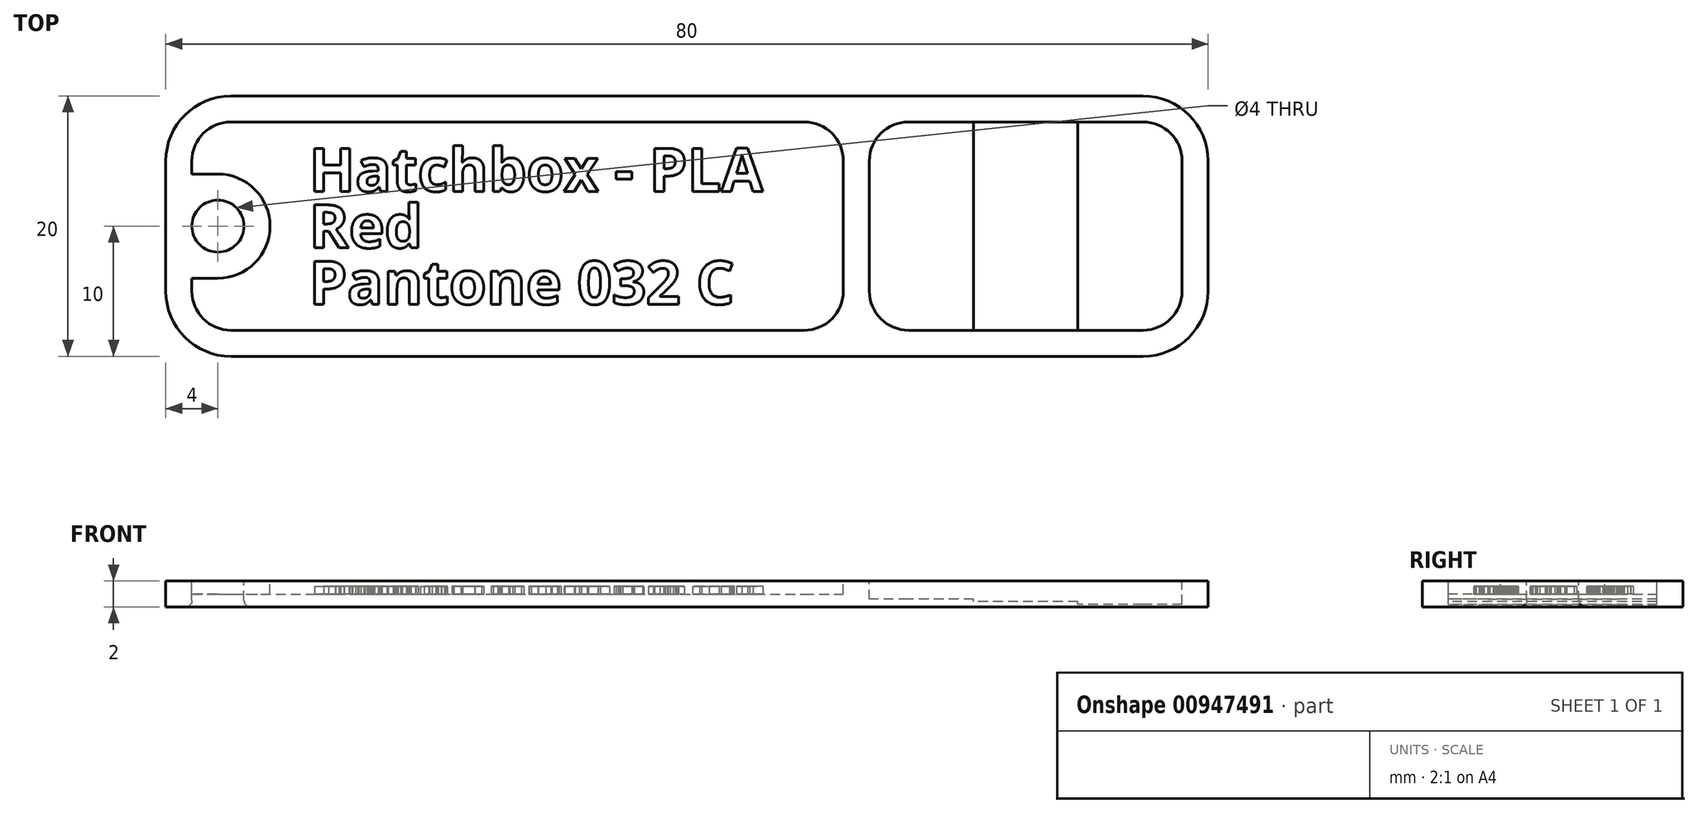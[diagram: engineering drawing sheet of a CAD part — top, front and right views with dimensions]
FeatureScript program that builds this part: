
annotation { "Feature Type Name" : "Feature", "Feature Type Description" : "" }
export const myFeature = defineFeature(function(context is Context, id is Id, definition is map)
    precondition{}
    {
        {
            var Q0;
            Q0=qCreatedBy(makeId("Top.planeOp"),FACE);
            var sketch = newSketch(context, id + "F0", { "sketchPlane" : qUnion([Q0])});
            skLineSegment(sketch, "E0.bottom", {"start": v(35, 10) * mm, "end": v(-35, 10) * mm});
            skLineSegment(sketch, "E0.top", {"start": v(35, -10) * mm, "end": v(-35, -10) * mm});
            skLineSegment(sketch, "E0.left", {"start": v(40, 5) * mm, "end": v(40, -5) * mm});
            skLineSegment(sketch, "E0.right", {"start": v(-40, 5) * mm, "end": v(-40, -5) * mm});
            skPoint(sketch, "E0.middle", {"position": v(0, 0) * mm});
            skPoint(sketch, "E1.visualSharp", {"position": v(-40, 10) * mm});
            skArc(sketch, "E1.filletArc", {"start": v(-35, 10) * mm, "mid": v(-38.54, 8.54) * mm, "end": v(-40, 5) * mm});
            skPoint(sketch, "E2.visualSharp", {"position": v(40, 10) * mm});
            skArc(sketch, "E2.filletArc", {"start": v(40, 5) * mm, "mid": v(38.54, 8.54) * mm, "end": v(35, 10) * mm});
            skPoint(sketch, "E3.visualSharp", {"position": v(40, -10) * mm});
            skArc(sketch, "E3.filletArc", {"start": v(35, -10) * mm, "mid": v(38.54, -8.54) * mm, "end": v(40, -5) * mm});
            skPoint(sketch, "E4.visualSharp", {"position": v(-40, -10) * mm});
            skArc(sketch, "E4.filletArc", {"start": v(-40, -5) * mm, "mid": v(-38.54, -8.54) * mm, "end": v(-35, -10) * mm});
            skSolve(sketch);
        }
        {
            var Q0;
            Q0=qSketchRegion(id+"F0",true);
            extrude(context, id + "F1", {"entities" : qUnion([Q0]), "offsetDistance" : 25 * mm, "depth" : 2 * mm});
        }
        {
            var Q0;
            Q0=makeQuery(id+"F1.opExtrude","CAP_FACE",FACE,{"disambiguationData":[OSD([sQuery(id+"F0.wireOp",EDGE,"E0.bottom"),sQuery(id+"F0.wireOp",EDGE,"E0.top"),sQuery(id+"F0.wireOp",EDGE,"E0.left"),sQuery(id+"F0.wireOp",EDGE,"E0.right"),sQuery(id+"F0.wireOp",EDGE,"E1.filletArc"),sQuery(id+"F0.wireOp",EDGE,"E2.filletArc"),sQuery(id+"F0.wireOp",EDGE,"E3.filletArc"),sQuery(id+"F0.wireOp",EDGE,"E4.filletArc")])],"isStart":false});
            var sketch = newSketch(context, id + "F2", { "sketchPlane" : qUnion([Q0])});
            skLineSegment(sketch, "E5.0", {"start": v(38, -5) * mm, "end": v(38, 5) * mm});
            skArc(sketch, "E5.1", {"start": v(35, -8) * mm, "mid": v(37.12, -7.12) * mm, "end": v(38, -5) * mm});
            skArc(sketch, "E5.2", {"start": v(38, 5) * mm, "mid": v(37.12, 7.12) * mm, "end": v(35, 8) * mm});
            skLineSegment(sketch, "E5.3", {"start": v(-35, -8) * mm, "end": v(9, -8) * mm});
            skLineSegment(sketch, "E5.4", {"start": v(35, 8) * mm, "end": v(17, 8) * mm});
            skArc(sketch, "E5.5", {"start": v(-35, 8) * mm, "mid": v(-37.12, 7.12) * mm, "end": v(-38, 5) * mm});
            skArc(sketch, "E5.7", {"start": v(-38, -5) * mm, "mid": v(-37.12, -7.12) * mm, "end": v(-35, -8) * mm});
            skCircle(sketch, "E6", {"center": v(-36, 0) * mm, "radius": 2 * mm, "construction": true});
            skArc(sketch, "E7.0", {"start": v(-36, -4) * mm, "mid": v(-32, 0) * mm, "end": v(-36, 4) * mm});
            skLineSegment(sketch, "E8", {"start": v(-38, -5) * mm, "end": v(-38, -4) * mm});
            skLineSegment(sketch, "E9", {"start": v(-36, 4) * mm, "end": v(-38, 4) * mm});
            skLineSegment(sketch, "E10", {"start": v(-36, -4) * mm, "end": v(-38, -4) * mm});
            skLineSegment(sketch, "E11.trimOffspring", {"start": v(-38, 4) * mm, "end": v(-38, 5) * mm});
            skArc(sketch, "E12", {"start": v(17, 8) * mm, "mid": v(14.88, 7.12) * mm, "end": v(14, 5) * mm});
            skArc(sketch, "E13", {"start": v(14, -5) * mm, "mid": v(14.88, -7.12) * mm, "end": v(17, -8) * mm});
            skLineSegment(sketch, "E14", {"start": v(14, -5) * mm, "end": v(14, 5) * mm});
            skArc(sketch, "E15", {"start": v(12, 5) * mm, "mid": v(11.12, 7.12) * mm, "end": v(9, 8) * mm});
            skArc(sketch, "E16", {"start": v(12, -5) * mm, "mid": v(11.12, -7.12) * mm, "end": v(9, -8) * mm});
            skLineSegment(sketch, "E17", {"start": v(12, -5) * mm, "end": v(12, 5) * mm});
            skLineSegment(sketch, "E18.trimOffspring", {"start": v(9, 8) * mm, "end": v(-35, 8) * mm});
            skLineSegment(sketch, "E19.trimOffspring", {"start": v(17, -8) * mm, "end": v(35, -8) * mm});
            skSolve(sketch);
        }
        {
            var Q0;
            Q0=qSketchRegion(id+"F2",true);
            extrude(context, id + "F3", {"entities" : qUnion([Q0]), "operationType" : NewBodyOperationType.REMOVE, "oppositeDirection" : true, "offsetDistance" : 25 * mm, "depth" : 1 * mm});
        }
        {
            var Q0;
            Q0=makeQuery(id+"F1.opExtrude","CAP_FACE",FACE,{"disambiguationData":[OSD([sQuery(id+"F0.wireOp",EDGE,"E0.bottom"),sQuery(id+"F0.wireOp",EDGE,"E0.top"),sQuery(id+"F0.wireOp",EDGE,"E0.left"),sQuery(id+"F0.wireOp",EDGE,"E0.right"),sQuery(id+"F0.wireOp",EDGE,"E1.filletArc"),sQuery(id+"F0.wireOp",EDGE,"E2.filletArc"),sQuery(id+"F0.wireOp",EDGE,"E3.filletArc"),sQuery(id+"F0.wireOp",EDGE,"E4.filletArc")])],"isStart":false});
            var sketch = newSketch(context, id + "F4", { "sketchPlane" : qUnion([Q0])});
            skCircle(sketch, "E20.0", {"center": v(-36, 0) * mm, "radius": 2 * mm});
            skSolve(sketch);
        }
        {
            var Q0;
            Q0=qSketchRegion(id+"F4",true);
            extrude(context, id + "F5", {"entities" : qUnion([Q0]), "operationType" : NewBodyOperationType.REMOVE, "endBound" : BoundingType.THROUGH_ALL, "oppositeDirection" : true, "depth" : 25 * mm});
        }
        {
            var Q0;
            Q0=makeQuery(id+"F5.boolean.opBoolean","COPY",EDGE,{"derivedFrom":makeQuery(id+"F5.opExtrude","CAP_EDGE",EDGE,{"disambiguationData":[OSD([sQuery(id+"F4.wireOp",EDGE,"E20.0")])],"isStart":true})});
            var Q1;
            Q1=makeQuery(id+"F5.boolean.opBoolean","INTERSECT",EDGE,{"derivedFrom":[makeQuery(id+"F1.opExtrude","CAP_FACE",FACE,{"disambiguationData":[OSD([sQuery(id+"F0.wireOp",EDGE,"E0.bottom"),sQuery(id+"F0.wireOp",EDGE,"E0.top"),sQuery(id+"F0.wireOp",EDGE,"E0.left"),sQuery(id+"F0.wireOp",EDGE,"E0.right"),sQuery(id+"F0.wireOp",EDGE,"E1.filletArc"),sQuery(id+"F0.wireOp",EDGE,"E2.filletArc"),sQuery(id+"F0.wireOp",EDGE,"E3.filletArc"),sQuery(id+"F0.wireOp",EDGE,"E4.filletArc")])],"isStart":true}),makeQuery(id+"F5.opExtrude","SWEPT_FACE",FACE,{"disambiguationData":[OSD([sQuery(id+"F4.wireOp",EDGE,"E20.0")])]})]});
            fillet(context, id + "F6", {"entities" : qUnion([Q0, Q1]), "radius" : .5 * mm, "tangentPropagation" : true, "allowEdgeOverflow" : false});
        }
        {
            var Q0;
            Q0=makeQuery(id+"F3.boolean.opBoolean","COPY",FACE,{"derivedFrom":makeQuery(id+"F3.opExtrude","CAP_FACE",FACE,{"disambiguationData":[OSD([sQuery(id+"F2.wireOp",EDGE,"E5.0"),sQuery(id+"F2.wireOp",EDGE,"E5.1"),sQuery(id+"F2.wireOp",EDGE,"E5.2"),sQuery(id+"F2.wireOp",EDGE,"E5.4"),sQuery(id+"F2.wireOp",EDGE,"E12"),sQuery(id+"F2.wireOp",EDGE,"E13"),sQuery(id+"F2.wireOp",EDGE,"E14"),sQuery(id+"F2.wireOp",EDGE,"E19.trimOffspring")])],"isStart":false})});
            extrude(context, id + "F7", {"entities" : qUnion([Q0]), "operationType" : NewBodyOperationType.REMOVE, "oppositeDirection" : true, "offsetDistance" : 25 * mm, "depth" : 0.4 * mm});
        }
        {
            var Q0;
            Q0=makeQuery(id+"F7.boolean.opBoolean","COPY",FACE,{"derivedFrom":makeQuery(id+"F7.opExtrude","CAP_FACE",FACE,{"disambiguationData":[OSD([sQuery(id+"F2.wireOp",EDGE,"E5.0"),sQuery(id+"F2.wireOp",EDGE,"E5.1"),sQuery(id+"F2.wireOp",EDGE,"E5.2"),sQuery(id+"F2.wireOp",EDGE,"E5.4"),sQuery(id+"F2.wireOp",EDGE,"E12"),sQuery(id+"F2.wireOp",EDGE,"E13"),sQuery(id+"F2.wireOp",EDGE,"E14"),sQuery(id+"F2.wireOp",EDGE,"E19.trimOffspring")])],"isStart":false})});
            var sketch = newSketch(context, id + "F8", { "sketchPlane" : qUnion([Q0])});
            skArc(sketch, "E21.0.0", {"start": v(35, -8) * mm, "mid": v(37.12, -7.12) * mm, "end": v(38, -5) * mm});
            skLineSegment(sketch, "E21.0.1", {"start": v(38, -5) * mm, "end": v(38, 5) * mm});
            skArc(sketch, "E21.0.2", {"start": v(38, 5) * mm, "mid": v(37.12, 7.12) * mm, "end": v(35, 8) * mm});
            skLineSegment(sketch, "E21.0.3", {"start": v(35, 8) * mm, "end": v(22, 8) * mm});
            skLineSegment(sketch, "E21.0.7", {"start": v(22, -8) * mm, "end": v(35, -8) * mm});
            skLineSegment(sketch, "E22", {"start": v(22, 8) * mm, "end": v(22, -8) * mm});
            skPoint(sketch, "E21.0.4.start.orphan", {"position": v(17, 8) * mm});
            skPoint(sketch, "E21.0.5.start.orphan", {"position": v(14, 5) * mm});
            skPoint(sketch, "E21.0.6.start.orphan", {"position": v(14, -5) * mm});
            skPoint(sketch, "E23.orphan", {"position": v(17, -8) * mm});
            skSolve(sketch);
        }
        {
            var Q0;
            Q0=qSketchRegion(id+"F8",true);
            extrude(context, id + "F9", {"entities" : qUnion([Q0]), "operationType" : NewBodyOperationType.REMOVE, "oppositeDirection" : true, "offsetDistance" : 25 * mm, "depth" : 0.2 * mm});
        }
        {
            var Q0;
            Q0=makeQuery(id+"F9.boolean.opBoolean","COPY",FACE,{"derivedFrom":makeQuery(id+"F9.opExtrude","CAP_FACE",FACE,{"disambiguationData":[OSD([sQuery(id+"F8.wireOp",EDGE,"E21.0.0"),sQuery(id+"F8.wireOp",EDGE,"E21.0.1"),sQuery(id+"F8.wireOp",EDGE,"E21.0.2"),sQuery(id+"F8.wireOp",EDGE,"E21.0.3"),sQuery(id+"F8.wireOp",EDGE,"E21.0.7"),sQuery(id+"F8.wireOp",EDGE,"E22")])],"isStart":false})});
            var sketch = newSketch(context, id + "F10", { "sketchPlane" : qUnion([Q0])});
            skLineSegment(sketch, "E24.0.0", {"start": v(35, 8) * mm, "end": v(30, 8) * mm});
            skLineSegment(sketch, "E24.0.2", {"start": v(30, -8) * mm, "end": v(35, -8) * mm});
            skArc(sketch, "E24.0.3", {"start": v(35, -8) * mm, "mid": v(37.12, -7.12) * mm, "end": v(38, -5) * mm});
            skLineSegment(sketch, "E24.0.4", {"start": v(38, -5) * mm, "end": v(38, 5) * mm});
            skArc(sketch, "E24.0.5", {"start": v(38, 5) * mm, "mid": v(37.12, 7.12) * mm, "end": v(35, 8) * mm});
            skLineSegment(sketch, "E25", {"start": v(30, 8) * mm, "end": v(30, -8) * mm});
            skPoint(sketch, "E24.0.1.end.orphan", {"position": v(22, -8) * mm});
            skPoint(sketch, "E26.orphan", {"position": v(22, 8) * mm});
            skSolve(sketch);
        }
        {
            var Q0;
            Q0=makeQuery(id+"F10.imprint","IMPRINT",FACE,{"disambiguationData":[TD([[makeQuery(id+"F10.imprint","IMPRINT",EDGE,{"derivedFrom":sQuery(id+"F10.wireOp",EDGE,"E24.0.0")}),1.0]])]});
            extrude(context, id + "F11", {"entities" : qUnion([Q0]), "operationType" : NewBodyOperationType.REMOVE, "oppositeDirection" : true, "offsetDistance" : 25 * mm, "depth" : 0.2 * mm});
        }
        {
            var Q0;
            Q0=makeQuery(id+"F3.boolean.opBoolean","COPY",FACE,{"derivedFrom":makeQuery(id+"F3.opExtrude","CAP_FACE",FACE,{"disambiguationData":[OSD([sQuery(id+"F2.wireOp",EDGE,"E5.3"),sQuery(id+"F2.wireOp",EDGE,"E5.5"),sQuery(id+"F2.wireOp",EDGE,"E5.7"),sQuery(id+"F2.wireOp",EDGE,"E7.0"),sQuery(id+"F2.wireOp",EDGE,"E8"),sQuery(id+"F2.wireOp",EDGE,"E9"),sQuery(id+"F2.wireOp",EDGE,"E10"),sQuery(id+"F2.wireOp",EDGE,"E11.trimOffspring"),sQuery(id+"F2.wireOp",EDGE,"E15"),sQuery(id+"F2.wireOp",EDGE,"E16"),sQuery(id+"F2.wireOp",EDGE,"E17"),sQuery(id+"F2.wireOp",EDGE,"E18.trimOffspring")])],"isStart":false})});
            var sketch = newSketch(context, id + "F12", { "sketchPlane" : qUnion([Q0])});
            skText(sketch, "E27", { "text": "Hatchbox - PLA", "fontName": "OpenSans-Bold.ttf"});
            skText(sketch, "E28", { "text": "Red", "fontName": "OpenSans-Bold.ttf"});
            skText(sketch, "E29", { "text": "Pantone 032 C", "fontName": "OpenSans-Bold.ttf"});
            skLineSegment(sketch, "E30", {"start": v(-27.83, 1.67) * mm, "end": v(-27.83, 2.67) * mm, "construction": true});
            skLineSegment(sketch, "E31", {"start": v(-26.66, -2.67) * mm, "end": v(-26.66, -1.67) * mm, "construction": true});
            skLineSegment(sketch, "E32.bottom", {"start": v(-31, 7) * mm, "end": v(10, 7) * mm, "construction": true});
            skLineSegment(sketch, "E32.top", {"start": v(-31, -7) * mm, "end": v(10, -7) * mm, "construction": true});
            skLineSegment(sketch, "E32.left", {"start": v(-31, 7) * mm, "end": v(-31, -7) * mm, "construction": true});
            skLineSegment(sketch, "E32.right", {"start": v(10, 7) * mm, "end": v(10, -7) * mm, "construction": true});
            skLineSegment(sketch, "E33", {"start": v(-13.47, 7) * mm, "end": v(-13.47, 8) * mm, "construction": true});
            skLineSegment(sketch, "E34", {"start": v(-13.67, -7) * mm, "end": v(-13.67, -8) * mm, "construction": true});
            skLineSegment(sketch, "E35", {"start": v(-32, 0) * mm, "end": v(-31, 0) * mm, "construction": true});
            skPoint(sketch, "E35.startSnap0", {"position": v(-31, 0) * mm});
            skLineSegment(sketch, "E36", {"start": v(-29, 4.33) * mm, "end": v(-31, 4.33) * mm, "construction": true});
            skLineSegment(sketch, "E37", {"start": v(10, 1.23) * mm, "end": v(12, 1.23) * mm, "construction": true});
            skLineSegment(sketch, "E38", {"start": v(-29, -0.54) * mm, "end": v(-31, -0.54) * mm, "construction": true});
            skLineSegment(sketch, "E39", {"start": v(-29, -4.33) * mm, "end": v(-31, -4.33) * mm, "construction": true});
            skLineSegment(sketch, "E40", {"start": v(-25.76, 6) * mm, "end": v(-25.76, 7) * mm, "construction": true});
            skLineSegment(sketch, "E41", {"start": v(-26.93, -6) * mm, "end": v(-26.93, -7) * mm, "construction": true});
            const initialGuessF12  = {"E27": [-0.029, 0.00267, 1, 0, 0.00333], "E28": [-0.029, -0.00167, 1, 0, 0.00333], "E29": [-0.029, -0.006, 1, 0, 0.00333]};
            skSetInitialGuess(sketch, initialGuessF12);
            skSolve(sketch);
        }
        {
            var Q0;
            Q0 = qSketchRegion(id + "F12", true);
            extrude(context, id + "F13", {"entities" : qUnion([Q0]), "operationType" : NewBodyOperationType.ADD, "depth" : 0.6 * mm, "offsetDistance" : 25 * mm});
        }
    });
